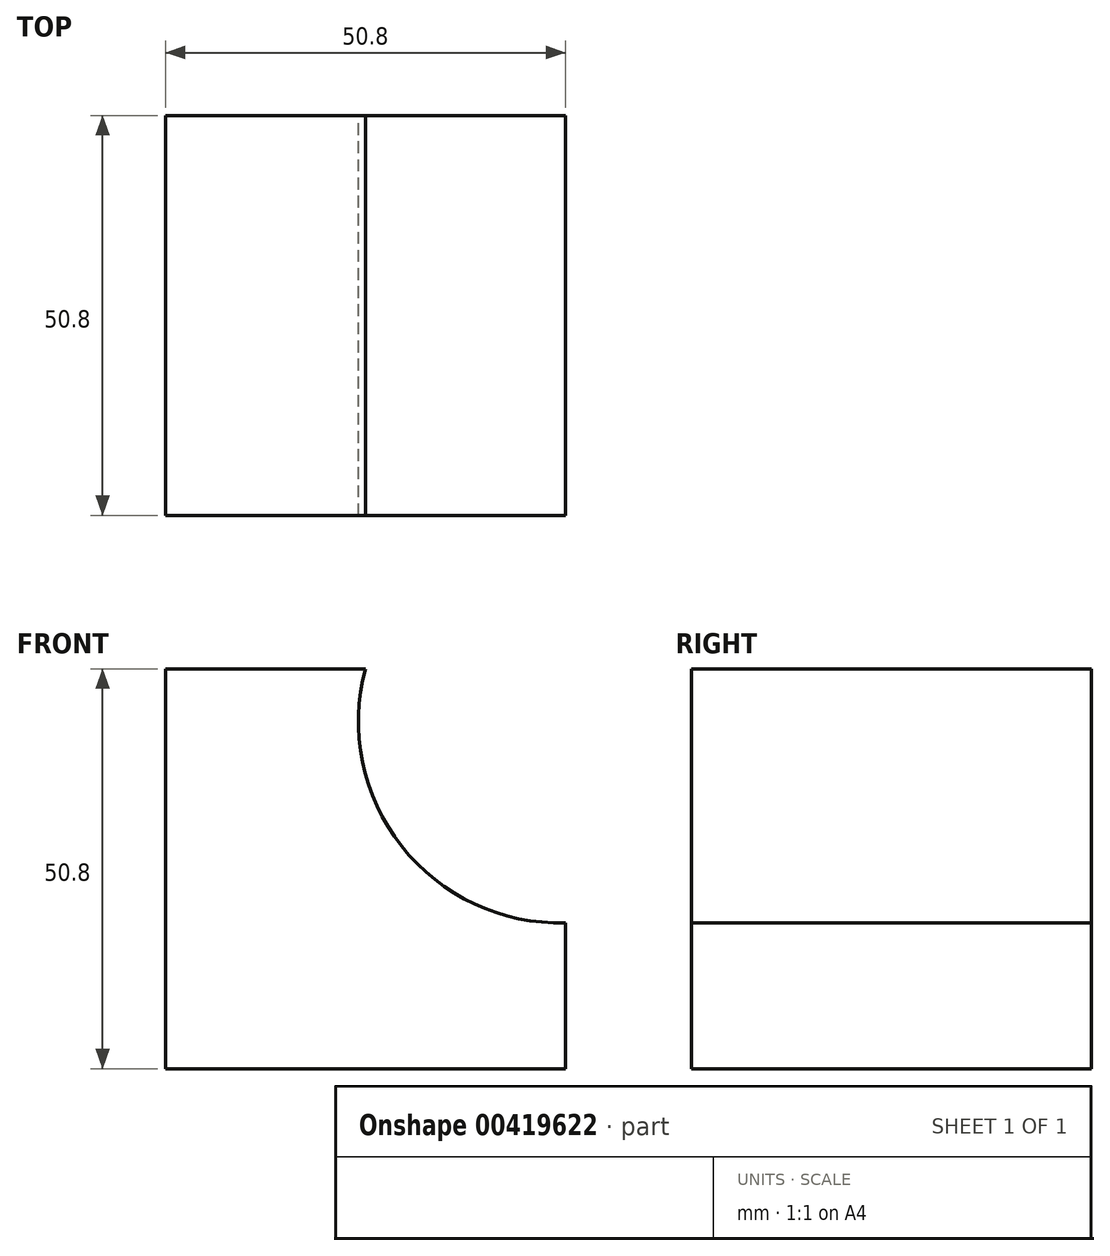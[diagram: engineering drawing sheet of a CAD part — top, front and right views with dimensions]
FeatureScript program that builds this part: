
annotation { "Feature Type Name" : "Feature", "Feature Type Description" : "" }
export const myFeature = defineFeature(function(context is Context, id is Id, definition is map)
    precondition{}
    {
        {
            var Q0;
            Q0=qCreatedBy(makeId("Front.planeOp"),FACE);
            var sketch = newSketch(context, id + "F0", { "sketchPlane" : qUnion([Q0])});
            skLineSegment(sketch, "E0", {"start": v(0, 0) * mm, "end": v(-50.8, 0) * mm});
            skLineSegment(sketch, "E1", {"start": v(-50.8, 0) * mm, "end": v(-50.8, 50.8) * mm});
            skLineSegment(sketch, "E2", {"start": v(-50.8, 50.8) * mm, "end": v(-25.4, 50.8) * mm});
            skLineSegment(sketch, "E3", {"start": v(0, 0) * mm, "end": v(0, 18.52) * mm});
            skArc(sketch, "E4", {"start": v(-25.4, 50.8) * mm, "mid": v(-20.83, 28.27) * mm, "end": v(0, 18.52) * mm});
            skSolve(sketch);
        }
        {
            var Q0;
            Q0=makeQuery(id+"F0.imprint","IMPRINT",FACE,{"disambiguationData":[TD([[makeQuery(id+"F0.imprint","IMPRINT",EDGE,{"derivedFrom":sQuery(id+"F0.wireOp",EDGE,"E0")}),-1.0]])]});
            extrude(context, id + "F1", {"entities" : qUnion([Q0]), "depth" : 50.8 * mm});
        }
    });
